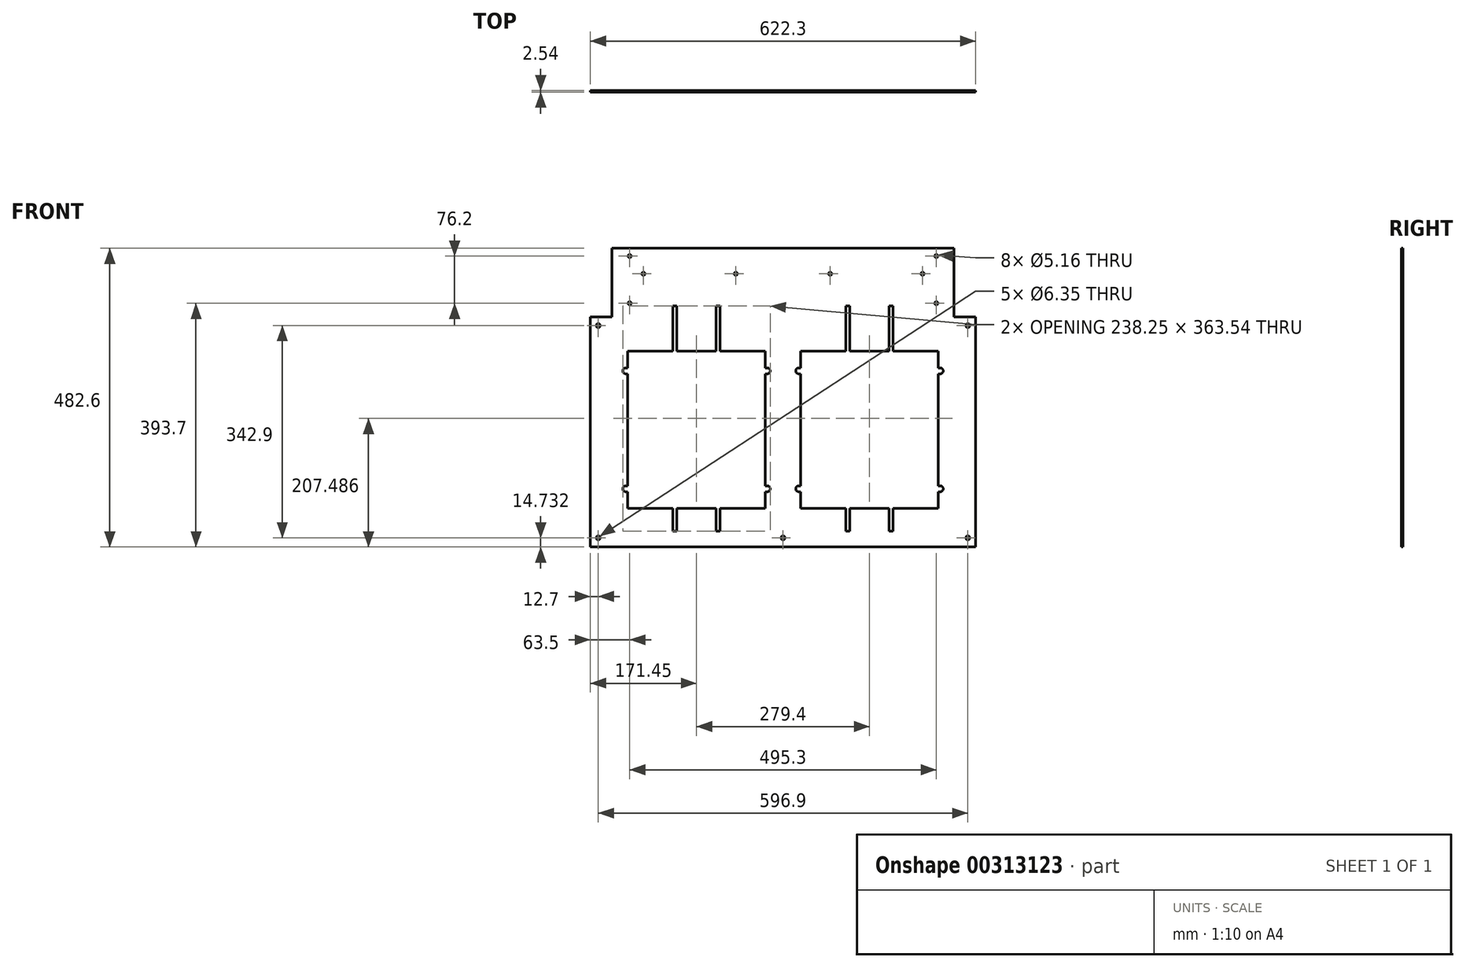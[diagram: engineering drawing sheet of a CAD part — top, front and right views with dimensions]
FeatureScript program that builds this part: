
annotation { "Feature Type Name" : "Feature", "Feature Type Description" : "" }
export const myFeature = defineFeature(function(context is Context, id is Id, definition is map)
    precondition{}
    {
        {
            var Q0;
            Q0=qCreatedBy(makeId("Front.planeOp"),FACE);
            var sketch = newSketch(context, id + "F0", { "sketchPlane" : qUnion([Q0])});
            skLineSegment(sketch, "E0.bottom", {"start": v(-622.3, 482.6) * mm, "end": v(0, 482.6) * mm});
            skLineSegment(sketch, "E0.top", {"start": v(-622.3, 0) * mm, "end": v(0, 0) * mm});
            skLineSegment(sketch, "E0.left", {"start": v(-622.3, 482.6) * mm, "end": v(-622.3, 0) * mm});
            skLineSegment(sketch, "E0.right", {"start": v(0, 482.6) * mm, "end": v(0, 0) * mm});
            skLineSegment(sketch, "E1.bottom", {"start": v(-561.98, 316.23) * mm, "end": v(-339.73, 316.23) * mm});
            skLineSegment(sketch, "E1.top", {"start": v(-561.98, 62.23) * mm, "end": v(-339.73, 62.23) * mm});
            skLineSegment(sketch, "E1.left", {"start": v(-561.98, 316.23) * mm, "end": v(-561.98, 289.3) * mm});
            skLineSegment(sketch, "E1.right", {"start": v(-339.73, 316.23) * mm, "end": v(-339.73, 289.3) * mm});
            skPoint(sketch, "E1.middle", {"position": v(-450.85, 189.23) * mm});
            skArc(sketch, "E2", {"start": v(-565.15, 289.3) * mm, "mid": v(-569.98, 284.48) * mm, "end": v(-565.15, 279.65) * mm});
            skArc(sketch, "E3", {"start": v(-336.55, 279.65) * mm, "mid": v(-331.72, 284.48) * mm, "end": v(-336.55, 289.3) * mm});
            skArc(sketch, "E4", {"start": v(-336.55, 89.15) * mm, "mid": v(-331.72, 93.98) * mm, "end": v(-336.55, 98.8) * mm});
            skArc(sketch, "E5", {"start": v(-565.15, 98.8) * mm, "mid": v(-569.98, 93.98) * mm, "end": v(-565.15, 89.15) * mm});
            skLineSegment(sketch, "E6", {"start": v(-336.55, 289.3) * mm, "end": v(-339.73, 289.3) * mm});
            skLineSegment(sketch, "E7", {"start": v(-336.55, 279.65) * mm, "end": v(-339.73, 279.65) * mm});
            skLineSegment(sketch, "E8.trimOffspring", {"start": v(-339.73, 279.65) * mm, "end": v(-339.73, 98.8) * mm});
            skLineSegment(sketch, "E9", {"start": v(-336.55, 98.8) * mm, "end": v(-339.73, 98.8) * mm});
            skLineSegment(sketch, "E10", {"start": v(-336.55, 89.15) * mm, "end": v(-339.73, 89.15) * mm});
            skLineSegment(sketch, "E11.trimOffspring", {"start": v(-339.73, 89.15) * mm, "end": v(-339.73, 62.23) * mm});
            skLineSegment(sketch, "E12", {"start": v(-565.15, 98.8) * mm, "end": v(-561.98, 98.8) * mm});
            skLineSegment(sketch, "E13", {"start": v(-565.15, 89.15) * mm, "end": v(-561.98, 89.15) * mm});
            skLineSegment(sketch, "E14", {"start": v(-565.15, 289.3) * mm, "end": v(-561.98, 289.3) * mm});
            skLineSegment(sketch, "E15", {"start": v(-565.15, 279.65) * mm, "end": v(-561.98, 279.65) * mm});
            skLineSegment(sketch, "E16.trimOffspring", {"start": v(-561.98, 279.65) * mm, "end": v(-561.98, 98.8) * mm});
            skLineSegment(sketch, "E17.trimOffspring", {"start": v(-561.98, 89.15) * mm, "end": v(-561.98, 62.23) * mm});
            skLineSegment(sketch, "E18.1.0.0", {"start": v(-282.58, 89.15) * mm, "end": v(-282.58, 62.23) * mm});
            skLineSegment(sketch, "E18.1.0.1", {"start": v(-60.33, 279.65) * mm, "end": v(-60.33, 98.8) * mm});
            skLineSegment(sketch, "E18.1.0.3", {"start": v(-60.33, 316.23) * mm, "end": v(-60.33, 289.3) * mm});
            skLineSegment(sketch, "E18.1.0.4", {"start": v(-60.33, 89.15) * mm, "end": v(-60.33, 62.23) * mm});
            skPoint(sketch, "E18.1.0.5", {"position": v(-171.45, 189.23) * mm});
            skLineSegment(sketch, "E18.1.0.6", {"start": v(-282.58, 316.23) * mm, "end": v(-60.33, 316.23) * mm});
            skLineSegment(sketch, "E18.1.0.7", {"start": v(-282.58, 62.23) * mm, "end": v(-60.33, 62.23) * mm});
            skLineSegment(sketch, "E18.1.0.8", {"start": v(-282.58, 279.65) * mm, "end": v(-282.58, 98.8) * mm});
            skLineSegment(sketch, "E18.1.0.9", {"start": v(-282.58, 316.23) * mm, "end": v(-282.58, 289.3) * mm});
            skLineSegment(sketch, "E18.1.0.10", {"start": v(-285.75, 98.8) * mm, "end": v(-282.58, 98.8) * mm});
            skLineSegment(sketch, "E18.1.0.11", {"start": v(-285.75, 289.3) * mm, "end": v(-282.58, 289.3) * mm});
            skArc(sketch, "E18.1.0.12", {"start": v(-57.15, 89.15) * mm, "mid": v(-52.32, 93.98) * mm, "end": v(-57.15, 98.8) * mm});
            skLineSegment(sketch, "E18.1.0.13", {"start": v(-57.15, 89.15) * mm, "end": v(-60.33, 89.15) * mm});
            skLineSegment(sketch, "E18.1.0.14", {"start": v(-285.75, 89.15) * mm, "end": v(-282.58, 89.15) * mm});
            skLineSegment(sketch, "E18.1.0.15", {"start": v(-57.15, 98.8) * mm, "end": v(-60.33, 98.8) * mm});
            skArc(sketch, "E18.1.0.16", {"start": v(-285.75, 98.8) * mm, "mid": v(-290.58, 93.98) * mm, "end": v(-285.75, 89.15) * mm});
            skLineSegment(sketch, "E18.1.0.17", {"start": v(-57.15, 289.3) * mm, "end": v(-60.33, 289.3) * mm});
            skLineSegment(sketch, "E18.1.0.18", {"start": v(-57.15, 279.65) * mm, "end": v(-60.33, 279.65) * mm});
            skArc(sketch, "E18.1.0.19", {"start": v(-57.15, 279.65) * mm, "mid": v(-52.32, 284.48) * mm, "end": v(-57.15, 289.3) * mm});
            skLineSegment(sketch, "E18.1.0.20", {"start": v(-285.75, 279.65) * mm, "end": v(-282.58, 279.65) * mm});
            skArc(sketch, "E18.1.0.21", {"start": v(-285.75, 289.3) * mm, "mid": v(-290.58, 284.48) * mm, "end": v(-285.75, 279.65) * mm});
            skLineSegment(sketch, "E18.direction1", {"start": v(-561.98, 62.23) * mm, "end": v(-282.58, 62.23) * mm, "construction": true});
            skCircle(sketch, "E19", {"center": v(-311.15, 14.73) * mm, "radius": 3.18 * mm});
            skPoint(sketch, "E19.centerSnap0", {"position": v(-311.15, 0) * mm});
            skCircle(sketch, "E20", {"center": v(-609.6, 14.73) * mm, "radius": 3.18 * mm});
            skCircle(sketch, "E21", {"center": v(-12.7, 14.73) * mm, "radius": 3.18 * mm});
            skCircle(sketch, "E22", {"center": v(-609.6, 357.63) * mm, "radius": 3.18 * mm});
            skCircle(sketch, "E23", {"center": v(-12.7, 357.63) * mm, "radius": 3.18 * mm});
            skCircle(sketch, "E24", {"center": v(-558.8, 469.9) * mm, "radius": 2.58 * mm});
            skCircle(sketch, "E25", {"center": v(-558.8, 393.7) * mm, "radius": 2.58 * mm});
            skCircle(sketch, "E26", {"center": v(-63.5, 469.9) * mm, "radius": 2.58 * mm});
            skCircle(sketch, "E27", {"center": v(-63.5, 393.7) * mm, "radius": 2.58 * mm});
            skSolve(sketch);
        }
        {
            var Q0;
            Q0=qSketchRegion(id+"F0",true);
            extrude(context, id + "F1", {"entities" : qUnion([Q0]), "endBound" : BoundingType.SYMMETRIC, "depth" : 2.54 * mm, "offsetDistance" : 25.4 * mm});
        }
        {
            var Q0;
            Q0=makeQuery(id+"F1.opExtrude","CAP_FACE",FACE,{"disambiguationData":[OSD([sQuery(id+"F0.wireOp",EDGE,"E0.bottom"),sQuery(id+"F0.wireOp",EDGE,"E0.top"),sQuery(id+"F0.wireOp",EDGE,"E0.left"),sQuery(id+"F0.wireOp",EDGE,"E0.right"),sQuery(id+"F0.wireOp",EDGE,"E1.bottom"),sQuery(id+"F0.wireOp",EDGE,"E1.top"),sQuery(id+"F0.wireOp",EDGE,"E1.left"),sQuery(id+"F0.wireOp",EDGE,"E1.right"),sQuery(id+"F0.wireOp",EDGE,"E2"),sQuery(id+"F0.wireOp",EDGE,"E3"),sQuery(id+"F0.wireOp",EDGE,"E4"),sQuery(id+"F0.wireOp",EDGE,"E5"),sQuery(id+"F0.wireOp",EDGE,"E6"),sQuery(id+"F0.wireOp",EDGE,"E7"),sQuery(id+"F0.wireOp",EDGE,"E8.trimOffspring"),sQuery(id+"F0.wireOp",EDGE,"E9"),sQuery(id+"F0.wireOp",EDGE,"E10"),sQuery(id+"F0.wireOp",EDGE,"E11.trimOffspring"),sQuery(id+"F0.wireOp",EDGE,"E12"),sQuery(id+"F0.wireOp",EDGE,"E13"),sQuery(id+"F0.wireOp",EDGE,"E14"),sQuery(id+"F0.wireOp",EDGE,"E15"),sQuery(id+"F0.wireOp",EDGE,"E16.trimOffspring"),sQuery(id+"F0.wireOp",EDGE,"E17.trimOffspring"),sQuery(id+"F0.wireOp",EDGE,"E18.1.0.0"),sQuery(id+"F0.wireOp",EDGE,"E18.1.0.1"),sQuery(id+"F0.wireOp",EDGE,"E18.1.0.3"),sQuery(id+"F0.wireOp",EDGE,"E18.1.0.4"),sQuery(id+"F0.wireOp",EDGE,"E18.1.0.6"),sQuery(id+"F0.wireOp",EDGE,"E18.1.0.7"),sQuery(id+"F0.wireOp",EDGE,"E18.1.0.8"),sQuery(id+"F0.wireOp",EDGE,"E18.1.0.9"),sQuery(id+"F0.wireOp",EDGE,"E18.1.0.10"),sQuery(id+"F0.wireOp",EDGE,"E18.1.0.11"),sQuery(id+"F0.wireOp",EDGE,"E18.1.0.12"),sQuery(id+"F0.wireOp",EDGE,"E18.1.0.13"),sQuery(id+"F0.wireOp",EDGE,"E18.1.0.14"),sQuery(id+"F0.wireOp",EDGE,"E18.1.0.15"),sQuery(id+"F0.wireOp",EDGE,"E18.1.0.16"),sQuery(id+"F0.wireOp",EDGE,"E18.1.0.17"),sQuery(id+"F0.wireOp",EDGE,"E18.1.0.18"),sQuery(id+"F0.wireOp",EDGE,"E18.1.0.19"),sQuery(id+"F0.wireOp",EDGE,"E18.1.0.20"),sQuery(id+"F0.wireOp",EDGE,"E18.1.0.21")])],"isStart":false});
            var sketch = newSketch(context, id + "F2", { "sketchPlane" : qUnion([Q0])});
            skLineSegment(sketch, "E28.bottom", {"start": v(-622.3, 482.6) * mm, "end": v(-587.38, 482.6) * mm});
            skLineSegment(sketch, "E28.top", {"start": v(-622.3, 371.47) * mm, "end": v(-587.38, 371.47) * mm});
            skLineSegment(sketch, "E28.left", {"start": v(-622.3, 482.6) * mm, "end": v(-622.3, 371.47) * mm});
            skLineSegment(sketch, "E28.right", {"start": v(-587.38, 482.6) * mm, "end": v(-587.38, 371.48) * mm});
            skLineSegment(sketch, "E29.bottom", {"start": v(0, 482.6) * mm, "end": v(-34.92, 482.6) * mm});
            skLineSegment(sketch, "E29.top", {"start": v(0, 371.48) * mm, "end": v(-34.92, 371.48) * mm});
            skLineSegment(sketch, "E29.left", {"start": v(0, 482.6) * mm, "end": v(0, 371.48) * mm});
            skLineSegment(sketch, "E29.right", {"start": v(-34.92, 482.6) * mm, "end": v(-34.92, 371.48) * mm});
            skLineSegment(sketch, "E30.bottom", {"start": v(-488.95, 316.23) * mm, "end": v(-482.6, 316.23) * mm});
            skLineSegment(sketch, "E30.top", {"start": v(-488.95, 389.26) * mm, "end": v(-482.6, 389.26) * mm});
            skLineSegment(sketch, "E30.left", {"start": v(-488.95, 316.23) * mm, "end": v(-488.95, 389.26) * mm});
            skLineSegment(sketch, "E30.right", {"start": v(-482.6, 316.23) * mm, "end": v(-482.6, 389.26) * mm});
            skLineSegment(sketch, "E31.bottom", {"start": v(-419.1, 316.23) * mm, "end": v(-412.75, 316.23) * mm});
            skLineSegment(sketch, "E31.top", {"start": v(-419.1, 389.26) * mm, "end": v(-412.75, 389.26) * mm});
            skLineSegment(sketch, "E31.left", {"start": v(-419.1, 316.23) * mm, "end": v(-419.1, 389.26) * mm});
            skLineSegment(sketch, "E31.right", {"start": v(-412.75, 316.23) * mm, "end": v(-412.75, 389.25) * mm});
            skLineSegment(sketch, "E32.bottom", {"start": v(-419.1, 62.23) * mm, "end": v(-412.75, 62.23) * mm});
            skLineSegment(sketch, "E32.top", {"start": v(-419.1, 25.72) * mm, "end": v(-412.75, 25.72) * mm});
            skLineSegment(sketch, "E32.left", {"start": v(-419.1, 62.23) * mm, "end": v(-419.1, 25.72) * mm});
            skLineSegment(sketch, "E32.right", {"start": v(-412.75, 62.23) * mm, "end": v(-412.75, 25.72) * mm});
            skLineSegment(sketch, "E33.bottom", {"start": v(-482.6, 62.23) * mm, "end": v(-488.95, 62.23) * mm});
            skLineSegment(sketch, "E33.top", {"start": v(-482.6, 25.72) * mm, "end": v(-488.95, 25.72) * mm});
            skLineSegment(sketch, "E33.left", {"start": v(-482.6, 62.23) * mm, "end": v(-482.6, 25.72) * mm});
            skLineSegment(sketch, "E33.right", {"start": v(-488.95, 62.23) * mm, "end": v(-488.95, 25.72) * mm});
            skLineSegment(sketch, "E34.1.0.0", {"start": v(-209.55, 316.23) * mm, "end": v(-209.55, 389.26) * mm});
            skLineSegment(sketch, "E34.1.0.1", {"start": v(-203.2, 316.23) * mm, "end": v(-203.2, 389.26) * mm});
            skLineSegment(sketch, "E34.1.0.2", {"start": v(-139.7, 62.23) * mm, "end": v(-139.7, 25.72) * mm});
            skLineSegment(sketch, "E34.1.0.3", {"start": v(-133.35, 62.23) * mm, "end": v(-133.35, 25.72) * mm});
            skLineSegment(sketch, "E34.1.0.4", {"start": v(-139.7, 316.23) * mm, "end": v(-139.7, 389.25) * mm});
            skLineSegment(sketch, "E34.1.0.5", {"start": v(-133.35, 316.23) * mm, "end": v(-133.35, 389.25) * mm});
            skLineSegment(sketch, "E34.1.0.6", {"start": v(-209.55, 62.23) * mm, "end": v(-209.55, 25.72) * mm});
            skLineSegment(sketch, "E34.1.0.7", {"start": v(-203.2, 62.23) * mm, "end": v(-203.2, 25.72) * mm});
            skLineSegment(sketch, "E34.1.0.8", {"start": v(-139.7, 25.72) * mm, "end": v(-133.35, 25.72) * mm});
            skLineSegment(sketch, "E34.1.0.9", {"start": v(-209.55, 389.26) * mm, "end": v(-203.2, 389.26) * mm});
            skLineSegment(sketch, "E34.1.0.10", {"start": v(-203.2, 62.23) * mm, "end": v(-209.55, 62.23) * mm});
            skLineSegment(sketch, "E34.1.0.11", {"start": v(-209.55, 316.23) * mm, "end": v(-203.2, 316.23) * mm});
            skLineSegment(sketch, "E34.1.0.12", {"start": v(-139.7, 316.23) * mm, "end": v(-133.35, 316.23) * mm});
            skLineSegment(sketch, "E34.1.0.13", {"start": v(-139.7, 389.26) * mm, "end": v(-133.35, 389.26) * mm});
            skLineSegment(sketch, "E34.1.0.14", {"start": v(-139.7, 62.23) * mm, "end": v(-133.35, 62.23) * mm});
            skLineSegment(sketch, "E34.1.0.15", {"start": v(-203.2, 25.72) * mm, "end": v(-209.55, 25.72) * mm});
            skLineSegment(sketch, "E34.direction1", {"start": v(-488.95, 25.72) * mm, "end": v(-209.55, 25.72) * mm, "construction": true});
            skPoint(sketch, "E35", {"position": v(-415.93, 316.23) * mm});
            skPoint(sketch, "E36", {"position": v(-485.78, 316.23) * mm});
            skCircle(sketch, "E37", {"center": v(-85.73, 441.33) * mm, "radius": 2.58 * mm});
            skCircle(sketch, "E38", {"center": v(-536.58, 441.32) * mm, "radius": 2.58 * mm});
            skLineSegment(sketch, "E39", {"start": v(-85.73, 441.32) * mm, "end": v(-536.58, 441.32) * mm, "construction": true});
            skPoint(sketch, "E40", {"position": v(-311.15, 441.32) * mm});
            skCircle(sketch, "E41", {"center": v(-234.95, 441.32) * mm, "radius": 2.58 * mm});
            skCircle(sketch, "E42", {"center": v(-387.35, 441.32) * mm, "radius": 2.58 * mm});
            skLineSegment(sketch, "E43.direction1", {"start": v(-536.58, 441.32) * mm, "end": v(-387.35, 441.32) * mm, "construction": true});
            skLineSegment(sketch, "E44.direction1", {"start": v(-536.58, 441.32) * mm, "end": v(-311.15, 441.32) * mm, "construction": true});
            skSolve(sketch);
        }
        {
            var Q0;
            Q0=qSketchRegion(id+"F2",true);
            extrude(context, id + "F3", {"entities" : qUnion([Q0]), "operationType" : NewBodyOperationType.REMOVE, "endBound" : BoundingType.THROUGH_ALL, "oppositeDirection" : true, "depth" : 25.4 * mm});
        }
    });
